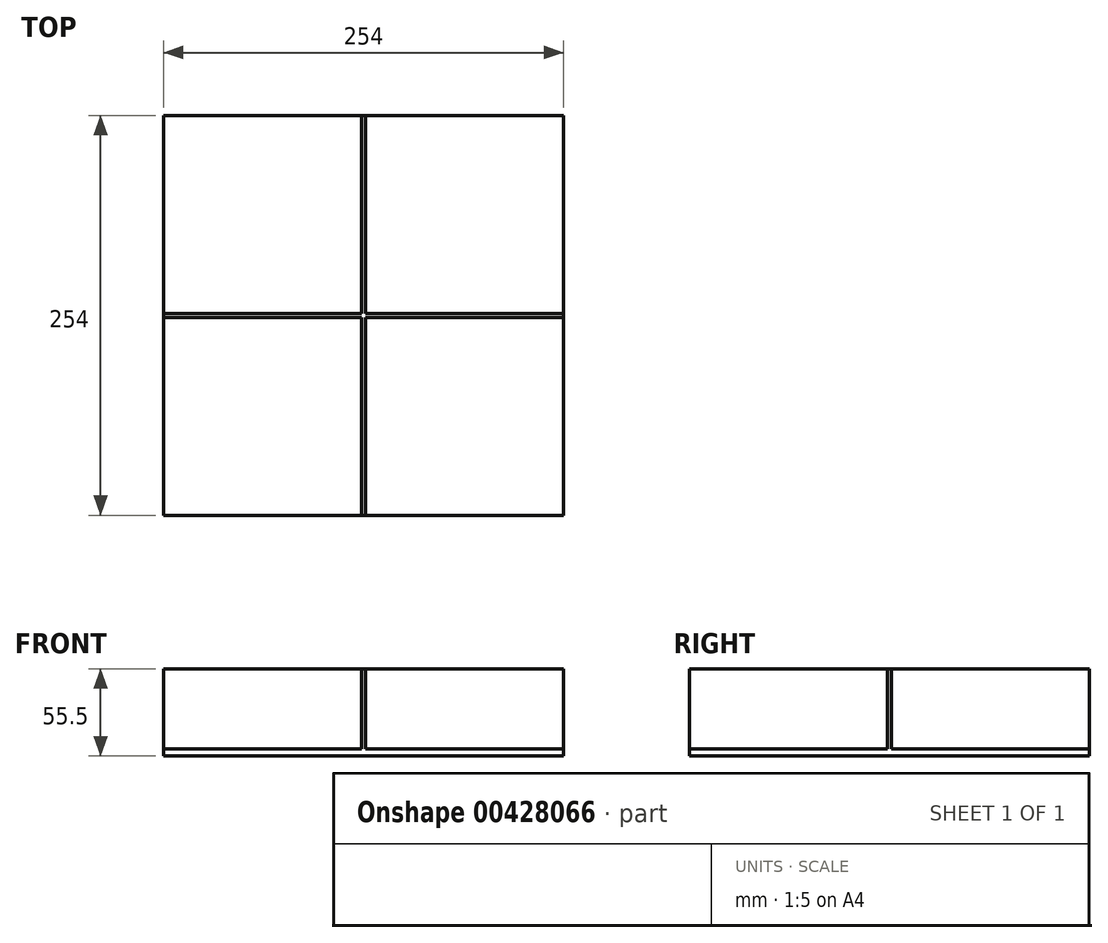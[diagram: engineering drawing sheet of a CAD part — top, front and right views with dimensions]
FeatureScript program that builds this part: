
annotation { "Feature Type Name" : "Feature", "Feature Type Description" : "" }
export const myFeature = defineFeature(function(context is Context, id is Id, definition is map)
    precondition{}
    {
        {
            var Q0;
            Q0=qCreatedBy(makeId("Top.planeOp"),FACE);
            var sketch = newSketch(context, id + "F0", { "sketchPlane" : qUnion([Q0])});
            skLineSegment(sketch, "E0.bottom", {"start": v(0, 0) * mm, "end": v(254, 0) * mm});
            skLineSegment(sketch, "E0.top", {"start": v(0, 254) * mm, "end": v(254, 254) * mm});
            skLineSegment(sketch, "E0.left", {"start": v(0, 0) * mm, "end": v(0, 254) * mm});
            skLineSegment(sketch, "E0.right", {"start": v(254, 0) * mm, "end": v(254, 254) * mm});
            skSolve(sketch);
        }
        {
            var Q0;
            Q0 = qSketchRegion(id + "F0", true);
            extrude(context, id + "F1", {"entities" : qUnion([Q0]), "depth" : 4.7 * mm});
        }
        {
            var Q0;
            Q0=makeQuery(id+"F1.opExtrude","CAP_FACE",FACE,{"disambiguationData":[OSD([sQuery(id+"F0.wireOp",EDGE,"E0.bottom"),sQuery(id+"F0.wireOp",EDGE,"E0.top"),sQuery(id+"F0.wireOp",EDGE,"E0.left"),sQuery(id+"F0.wireOp",EDGE,"E0.right")])],"isStart":false});
            var sketch = newSketch(context, id + "F2", { "sketchPlane" : qUnion([Q0])});
            skLineSegment(sketch, "E1", {"start": v(127, 254) * mm, "end": v(127, 0) * mm, "construction": true});
            skLineSegment(sketch, "E2", {"start": v(0, 127) * mm, "end": v(254, 127) * mm, "construction": true});
            skLineSegment(sketch, "E3.0", {"start": v(125.73, 254) * mm, "end": v(125.73, 128.27) * mm});
            skLineSegment(sketch, "E4.0", {"start": v(128.27, 254) * mm, "end": v(128.27, 128.27) * mm});
            skLineSegment(sketch, "E5.0", {"start": v(0, 128.27) * mm, "end": v(125.73, 128.27) * mm});
            skLineSegment(sketch, "E6.0", {"start": v(0, 125.73) * mm, "end": v(125.73, 125.73) * mm});
            skLineSegment(sketch, "E7.trimOffspring", {"start": v(128.27, 128.27) * mm, "end": v(254, 128.27) * mm});
            skLineSegment(sketch, "E8.trimOffspring", {"start": v(125.73, 125.73) * mm, "end": v(125.73, 0) * mm});
            skLineSegment(sketch, "E9.trimOffspring", {"start": v(128.27, 125.73) * mm, "end": v(254, 125.73) * mm});
            skLineSegment(sketch, "E10.trimOffspring", {"start": v(128.27, 125.73) * mm, "end": v(128.27, 0) * mm});
            skSolve(sketch);
        }
        {
            var Q0;
            Q0 = qSketchRegion(id + "F2", true);
            var Q1;
            {var subQ5=sQuery(id+"F2.wireOp",EDGE,"E3.0");Q1=makeQuery(id+"F2.imprint","IMPRINT",FACE,{"disambiguationData":[TD([[makeQuery(id+"F2.imprint","IMPRINT",EDGE,{"derivedFrom":subQ5}),1.0]])]});}
            extrude(context, id + "F3", {"entities" : qUnion([Q0, Q1]), "operationType" : NewBodyOperationType.ADD, "depth" : 50.8 * mm});
        }
    });
